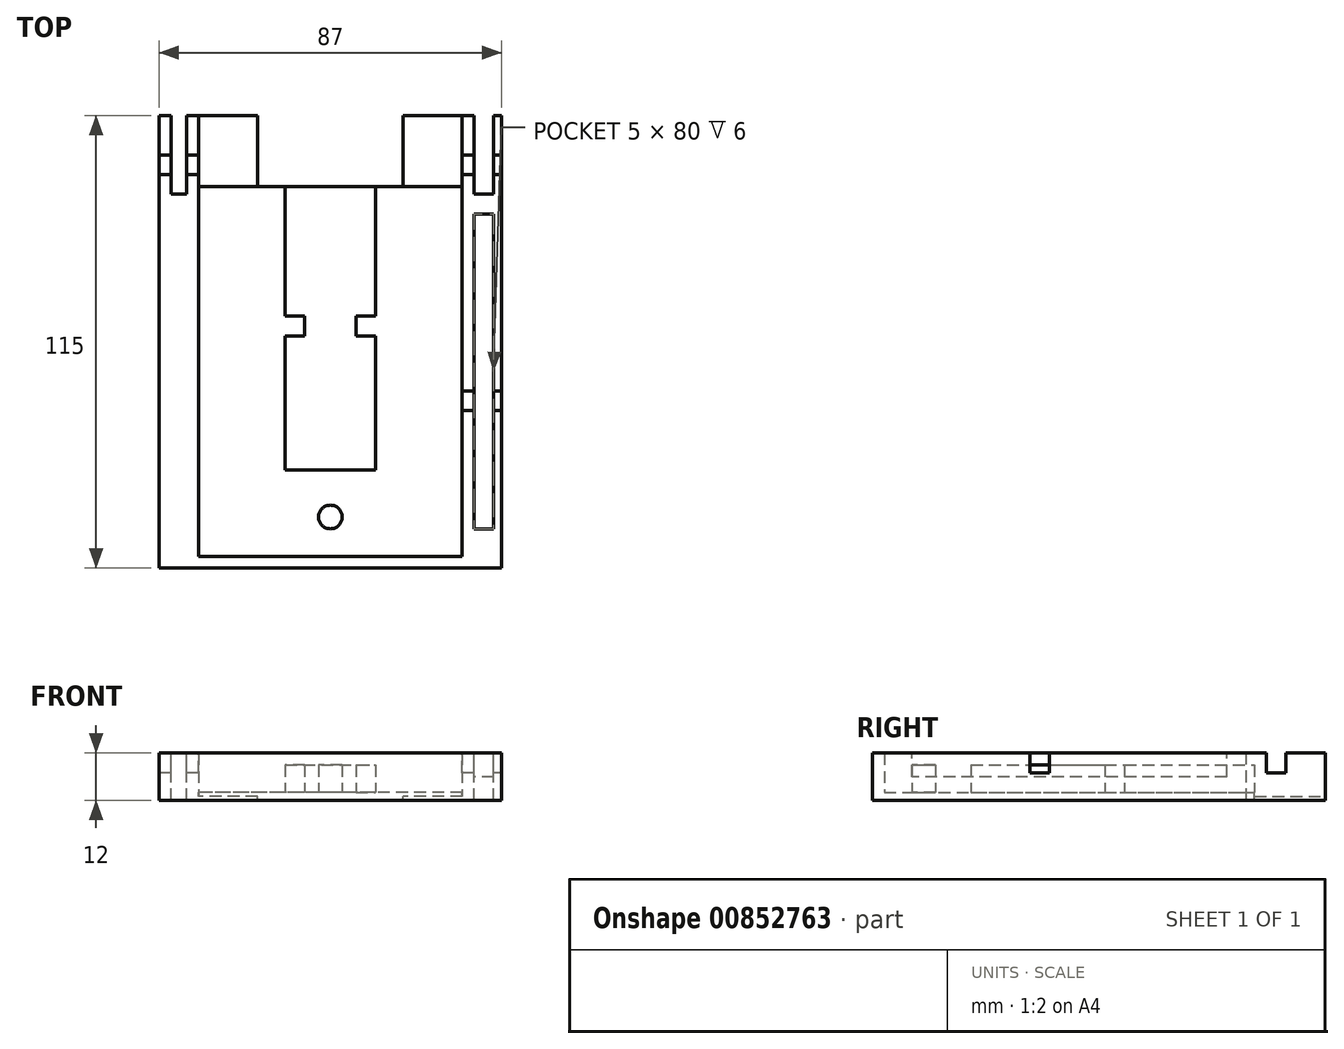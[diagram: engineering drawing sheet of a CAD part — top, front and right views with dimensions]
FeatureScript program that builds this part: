
annotation { "Feature Type Name" : "Feature", "Feature Type Description" : "" }
export const myFeature = defineFeature(function(context is Context, id is Id, definition is map)
    precondition{}
    {
        {
            var Q0;
            Q0=qCreatedBy(makeId("Top.planeOp"),FACE);
            var sketch = newSketch(context, id + "F0", { "sketchPlane" : qUnion([Q0])});
            skLineSegment(sketch, "E0.bottom", {"start": v(43.5, -57.5) * mm, "end": v(-43.5, -57.5) * mm});
            skLineSegment(sketch, "E0.top", {"start": v(43.5, 57.5) * mm, "end": v(-43.5, 57.5) * mm});
            skLineSegment(sketch, "E0.left", {"start": v(43.5, -57.5) * mm, "end": v(43.5, 57.5) * mm});
            skLineSegment(sketch, "E0.right", {"start": v(-43.5, -57.5) * mm, "end": v(-43.5, 57.5) * mm});
            skPoint(sketch, "E0.middle", {"position": v(0, 0) * mm});
            skSolve(sketch);
        }
        {
            var Q0;
            Q0=makeQuery(id+"F0.imprint","IMPRINT",FACE,{"disambiguationData":[TD([[makeQuery(id+"F0.imprint","IMPRINT",EDGE,{"derivedFrom":sQuery(id+"F0.wireOp",EDGE,"E0.bottom")}),-1.0]])]});
            extrude(context, id + "F1", {"entities" : qUnion([Q0]), "depth" : 2 * mm, "offsetDistance" : 25 * mm});
        }
        {
            var Q0;
            Q0=makeQuery(id+"F1.opExtrude","CAP_FACE",FACE,{"disambiguationData":[OSD([sQuery(id+"F0.wireOp",EDGE,"E0.bottom"),sQuery(id+"F0.wireOp",EDGE,"E0.top"),sQuery(id+"F0.wireOp",EDGE,"E0.left"),sQuery(id+"F0.wireOp",EDGE,"E0.right")])],"isStart":false});
            var sketch = newSketch(context, id + "F2", { "sketchPlane" : qUnion([Q0])});
            skLineSegment(sketch, "E1.0", {"start": v(-33.5, -54.5) * mm, "end": v(-33.5, 57.5) * mm});
            skLineSegment(sketch, "E2.0", {"start": v(33.5, -54.5) * mm, "end": v(-33.5, -54.5) * mm});
            skLineSegment(sketch, "E3.0", {"start": v(33.5, -54.5) * mm, "end": v(33.5, 57.5) * mm});
            skLineSegment(sketch, "E4", {"start": v(0, -54.5) * mm, "end": v(0, -44.5) * mm, "construction": true});
            skCircle(sketch, "E5", {"center": v(0, -44.5) * mm, "radius": 3 * mm});
            skLineSegment(sketch, "E6.0", {"start": v(11.5, -32.5) * mm, "end": v(-11.5, -32.5) * mm});
            skLineSegment(sketch, "E7.0", {"start": v(-11.5, -32.5) * mm, "end": v(-11.5, 1.5) * mm});
            skLineSegment(sketch, "E8.0", {"start": v(11.5, -32.5) * mm, "end": v(11.5, 1.5) * mm});
            skLineSegment(sketch, "E9", {"start": v(6.5, 1.5) * mm, "end": v(6.5, 6.5) * mm});
            skLineSegment(sketch, "E10", {"start": v(-6.5, 1.5) * mm, "end": v(-6.5, 6.5) * mm});
            skLineSegment(sketch, "E11", {"start": v(6.5, 1.5) * mm, "end": v(11.5, 1.5) * mm});
            skLineSegment(sketch, "E12", {"start": v(-6.5, 1.5) * mm, "end": v(-11.5, 1.5) * mm});
            skLineSegment(sketch, "E13", {"start": v(-6.5, 6.5) * mm, "end": v(-11.5, 6.5) * mm});
            skLineSegment(sketch, "E14", {"start": v(6.5, 6.5) * mm, "end": v(11.5, 6.5) * mm});
            skPoint(sketch, "E15.endSnap0", {"position": v(-9, 1.5) * mm});
            skLineSegment(sketch, "E16", {"start": v(6.5, 1.5) * mm, "end": v(6.5, -32.5) * mm, "construction": true});
            skLineSegment(sketch, "E17", {"start": v(-6.5, 1.5) * mm, "end": v(-6.5, -32.5) * mm, "construction": true});
            skLineSegment(sketch, "E18.trimOffspring", {"start": v(-11.5, 6.5) * mm, "end": v(-11.5, 39.5) * mm});
            skLineSegment(sketch, "E19.trimOffspring", {"start": v(11.5, 6.5) * mm, "end": v(11.5, 39.5) * mm});
            skLineSegment(sketch, "E20", {"start": v(-11.5, 39.5) * mm, "end": v(11.5, 39.5) * mm});
            skLineSegment(sketch, "E21", {"start": v(11.5, 39.5) * mm, "end": v(33.5, 39.5) * mm});
            skLineSegment(sketch, "E22", {"start": v(-11.5, 39.5) * mm, "end": v(-33.5, 39.5) * mm});
            skLineSegment(sketch, "E23", {"start": v(-18.5, 39.5) * mm, "end": v(-18.5, 57.5) * mm});
            skLineSegment(sketch, "E24", {"start": v(-33.5, 54.3) * mm, "end": v(-18.5, 54.3) * mm, "construction": true});
            skLineSegment(sketch, "E25", {"start": v(18.5, 39.5) * mm, "end": v(18.5, 57.5) * mm});
            skLineSegment(sketch, "E26", {"start": v(18.5, 51.79) * mm, "end": v(33.5, 51.79) * mm, "construction": true});
            skSolve(sketch);
        }
        {
            var Q0;
            {var subQ1=sQuery(id+"F2.wireOp",EDGE,"E1.0");Q0=makeQuery(id+"F2.imprint","IMPRINT",FACE,{"disambiguationData":[TD([[makeQuery(id+"F2.imprint","IMPRINT",EDGE,{"derivedFrom":subQ1}),1.0]])]});}
            extrude(context, id + "F3", {"entities" : qUnion([Q0]), "operationType" : NewBodyOperationType.ADD, "depth" : 10 * mm, "offsetDistance" : 25 * mm});
        }
        {
            var Q0;
            Q0=makeQuery(id+"F2.imprint","IMPRINT",FACE,{"disambiguationData":[TD([[makeQuery(id+"F2.imprint","IMPRINT",EDGE,{"derivedFrom":sQuery(id+"F2.wireOp",EDGE,"E5")}),1.0]])]});
            extrude(context, id + "F4", {"entities" : qUnion([Q0]), "operationType" : NewBodyOperationType.ADD, "depth" : 7 * mm, "offsetDistance" : 25 * mm});
        }
        {
            var Q0;
            Q0=makeQuery(id+"F2.imprint","IMPRINT",FACE,{"disambiguationData":[TD([[makeQuery(id+"F2.imprint","IMPRINT",EDGE,{"derivedFrom":sQuery(id+"F2.wireOp",EDGE,"E6.0")}),-1.0]])]});
            extrude(context, id + "F5", {"entities" : qUnion([Q0]), "operationType" : NewBodyOperationType.ADD, "depth" : 7 * mm, "offsetDistance" : 25 * mm});
        }
        {
            var Q0;
            Q0=makeQuery(id+"F3.opExtrude","CAP_FACE",FACE,{"disambiguationData":[OSD([sQuery(id+"F0.wireOp",EDGE,"E0.bottom"),sQuery(id+"F0.wireOp",EDGE,"E0.top"),sQuery(id+"F0.wireOp",EDGE,"E0.left"),sQuery(id+"F0.wireOp",EDGE,"E0.right"),sQuery(id+"F2.wireOp",EDGE,"E1.0"),sQuery(id+"F2.wireOp",EDGE,"E2.0"),sQuery(id+"F2.wireOp",EDGE,"E3.0")])],"isStart":false});
            var sketch = newSketch(context, id + "F6", { "sketchPlane" : qUnion([Q0])});
            skLineSegment(sketch, "E27", {"start": v(41.5, 57.5) * mm, "end": v(41.5, 32.5) * mm, "construction": true});
            skLineSegment(sketch, "E28", {"start": v(41.5, -47.5) * mm, "end": v(41.5, -57.5) * mm, "construction": true});
            skLineSegment(sketch, "E29", {"start": v(41.5, 32.5) * mm, "end": v(41.5, -57.5) * mm, "construction": true});
            skLineSegment(sketch, "E30", {"start": v(41.5, 32.5) * mm, "end": v(43.5, 32.5) * mm, "construction": true});
            skLineSegment(sketch, "E31.bottom", {"start": v(41.5, 32.5) * mm, "end": v(36.5, 32.5) * mm});
            skLineSegment(sketch, "E31.top", {"start": v(41.5, -47.5) * mm, "end": v(36.5, -47.5) * mm});
            skLineSegment(sketch, "E31.left", {"start": v(41.5, 32.5) * mm, "end": v(41.5, -47.5) * mm});
            skLineSegment(sketch, "E31.right", {"start": v(36.5, 32.5) * mm, "end": v(36.5, -47.5) * mm});
            skLineSegment(sketch, "E32", {"start": v(36.5, 57.5) * mm, "end": v(36.5, 37.5) * mm});
            skLineSegment(sketch, "E33", {"start": v(36.5, 37.5) * mm, "end": v(41.5, 37.5) * mm});
            skLineSegment(sketch, "E34", {"start": v(41.5, 37.5) * mm, "end": v(41.5, 57.5) * mm});
            skLineSegment(sketch, "E35", {"start": v(41.5, 37.5) * mm, "end": v(43.5, 37.5) * mm, "construction": true});
            skLineSegment(sketch, "E36", {"start": v(-40.5, 57.5) * mm, "end": v(-40.5, 37.5) * mm});
            skLineSegment(sketch, "E37", {"start": v(-40.5, 37.5) * mm, "end": v(-36.5, 37.5) * mm});
            skLineSegment(sketch, "E38", {"start": v(-36.5, 37.5) * mm, "end": v(-36.5, 57.5) * mm});
            skLineSegment(sketch, "E39", {"start": v(-40.5, 37.5) * mm, "end": v(-43.5, 37.5) * mm, "construction": true});
            skLineSegment(sketch, "E40.0", {"start": v(-33.5, 47.5) * mm, "end": v(-36.5, 47.5) * mm});
            skLineSegment(sketch, "E41.0", {"start": v(-33.5, 42.5) * mm, "end": v(-36.5, 42.5) * mm});
            skLineSegment(sketch, "E42.trimOffspring", {"start": v(-40.5, 47.5) * mm, "end": v(-43.5, 47.5) * mm});
            skLineSegment(sketch, "E43.trimOffspring", {"start": v(-40.5, 42.5) * mm, "end": v(-43.5, 42.5) * mm});
            skLineSegment(sketch, "E44.0", {"start": v(43.5, 47.5) * mm, "end": v(33.5, 47.5) * mm});
            skLineSegment(sketch, "E45.0", {"start": v(43.5, 42.5) * mm, "end": v(33.5, 42.5) * mm});
            skLineSegment(sketch, "E46.0", {"start": v(43.5, 52.5) * mm, "end": v(33.5, 52.5) * mm});
            skLineSegment(sketch, "E47", {"start": v(33.5, -17.5) * mm, "end": v(36.5, -17.5) * mm});
            skLineSegment(sketch, "E48", {"start": v(35.02, -17.5) * mm, "end": v(35.02, -57.5) * mm, "construction": true});
            skLineSegment(sketch, "E49.0", {"start": v(33.5, -12.5) * mm, "end": v(36.5, -12.5) * mm});
            skLineSegment(sketch, "E50.trimOffspring", {"start": v(41.5, -12.5) * mm, "end": v(43.5, -12.5) * mm});
            skLineSegment(sketch, "E51.trimOffspring", {"start": v(41.5, -17.5) * mm, "end": v(43.5, -17.5) * mm});
            skSolve(sketch);
        }
        {
            var Q0;
            Q0=makeQuery(id+"F2.imprint","IMPRINT",FACE,{"disambiguationData":[TD([[makeQuery(id+"F2.imprint","IMPRINT",EDGE,{"derivedFrom":sQuery(id+"F2.wireOp",EDGE,"E20")}),1.0]])]});
            extrude(context, id + "F7", {"entities" : qUnion([Q0]), "operationType" : NewBodyOperationType.REMOVE, "oppositeDirection" : true, "depth" : 25 * mm, "offsetDistance" : 25 * mm});
        }
        {
            var Q0;
            Q0=makeQuery(id+"F6.imprint","IMPRINT",FACE,{"disambiguationData":[TD([[makeQuery(id+"F6.imprint","IMPRINT",EDGE,{"derivedFrom":sQuery(id+"F6.wireOp",EDGE,"E31.bottom")}),1.0]])]});
            extrude(context, id + "F8", {"entities" : qUnion([Q0]), "operationType" : NewBodyOperationType.REMOVE, "oppositeDirection" : true, "depth" : 6 * mm, "offsetDistance" : 25 * mm});
        }
        {
            var Q0;
            {var subQ0=sQuery(id+"F6.wireOp",EDGE,"E36");Q0=makeQuery(id+"F6.imprint","IMPRINT",FACE,{"disambiguationData":[TD([[makeQuery(id+"F6.imprint","IMPRINT",EDGE,{"derivedFrom":subQ0}),1.0]])]});}
            var Q1;
            {var subQ0=sQuery(id+"F6.wireOp",EDGE,"E32");Q1=makeQuery(id+"F6.imprint","IMPRINT",FACE,{"disambiguationData":[TD([[makeQuery(id+"F6.imprint","IMPRINT",EDGE,{"derivedFrom":subQ0}),1.0]])]});}
            extrude(context, id + "F9", {"entities" : qUnion([Q0, Q1]), "operationType" : NewBodyOperationType.REMOVE, "oppositeDirection" : true, "depth" : 25 * mm, "offsetDistance" : 25 * mm});
        }
        {
            var Q0;
            {var subQ0=sQuery(id+"F6.wireOp",EDGE,"E42.trimOffspring");Q0=makeQuery(id+"F6.imprint","IMPRINT",FACE,{"disambiguationData":[TD([[makeQuery(id+"F6.imprint","IMPRINT",EDGE,{"derivedFrom":subQ0}),1.0]])]});}
            var Q1;
            {var subQ0=sQuery(id+"F6.wireOp",EDGE,"E40.0");Q1=makeQuery(id+"F6.imprint","IMPRINT",FACE,{"disambiguationData":[TD([[makeQuery(id+"F6.imprint","IMPRINT",EDGE,{"derivedFrom":subQ0}),1.0]])]});}
            extrude(context, id + "F10", {"entities" : qUnion([Q0, Q1]), "operationType" : NewBodyOperationType.REMOVE, "oppositeDirection" : true, "depth" : 5 * mm, "offsetDistance" : 25 * mm});
        }
        {
            var Q0;
            {var subQ5=sQuery(id+"F2.wireOp",EDGE,"E23");Q0=makeQuery(id+"F2.imprint","IMPRINT",FACE,{"disambiguationData":[TD([[makeQuery(id+"F2.imprint","IMPRINT",EDGE,{"derivedFrom":subQ5}),1.0]])]});}
            var Q1;
            {var subQ5=sQuery(id+"F2.wireOp",EDGE,"E25");Q1=makeQuery(id+"F2.imprint","IMPRINT",FACE,{"disambiguationData":[TD([[makeQuery(id+"F2.imprint","IMPRINT",EDGE,{"derivedFrom":subQ5}),-1.0]])]});}
            extrude(context, id + "F11", {"entities" : qUnion([Q0, Q1]), "operationType" : NewBodyOperationType.REMOVE, "oppositeDirection" : true, "depth" : 1 * mm, "offsetDistance" : 25 * mm});
        }
        {
            var Q0;
            {var subQ0=sQuery(id+"F6.wireOp",EDGE,"E44.0");var subQ1=sQuery(id+"F6.wireOp",EDGE,"E32");var subQ2=makeQuery(id+"F6.imprint","INTERSECT",VERTEX,{"derivedFrom":[subQ1,subQ0]});Q0=makeQuery(id+"F6.imprint","IMPRINT",FACE,{"disambiguationData":[TD([[makeQuery(id+"F6.imprint","IMPRINT",EDGE,{"disambiguationData":[TD([[subQ2,-1.0]])],"derivedFrom":subQ1}),-1.0]])]});}
            var Q1;
            {var subQ0=sQuery(id+"F6.wireOp",EDGE,"E45.0");var subQ1=sQuery(id+"F6.wireOp",EDGE,"E34");var subQ2=makeQuery(id+"F6.imprint","INTERSECT",VERTEX,{"derivedFrom":[subQ1,subQ0]});Q1=makeQuery(id+"F6.imprint","IMPRINT",FACE,{"disambiguationData":[TD([[makeQuery(id+"F6.imprint","IMPRINT",EDGE,{"disambiguationData":[TD([[subQ2,-1.0]])],"derivedFrom":subQ1}),-1.0]])]});}
            extrude(context, id + "F12", {"entities" : qUnion([Q0, Q1]), "operationType" : NewBodyOperationType.REMOVE, "oppositeDirection" : true, "depth" : 5 * mm, "offsetDistance" : 25 * mm});
        }
        {
            var Q0;
            {var subQ0=sQuery(id+"F6.wireOp",EDGE,"E47");Q0=makeQuery(id+"F6.imprint","IMPRINT",FACE,{"disambiguationData":[TD([[makeQuery(id+"F6.imprint","IMPRINT",EDGE,{"derivedFrom":subQ0}),1.0]])]});}
            var Q1;
            {var subQ0=sQuery(id+"F6.wireOp",EDGE,"E50.trimOffspring");Q1=makeQuery(id+"F6.imprint","IMPRINT",FACE,{"disambiguationData":[TD([[makeQuery(id+"F6.imprint","IMPRINT",EDGE,{"derivedFrom":subQ0}),-1.0]])]});}
            extrude(context, id + "F13", {"entities" : qUnion([Q0, Q1]), "operationType" : NewBodyOperationType.REMOVE, "oppositeDirection" : true, "depth" : 5 * mm, "offsetDistance" : 25 * mm});
        }
    });
